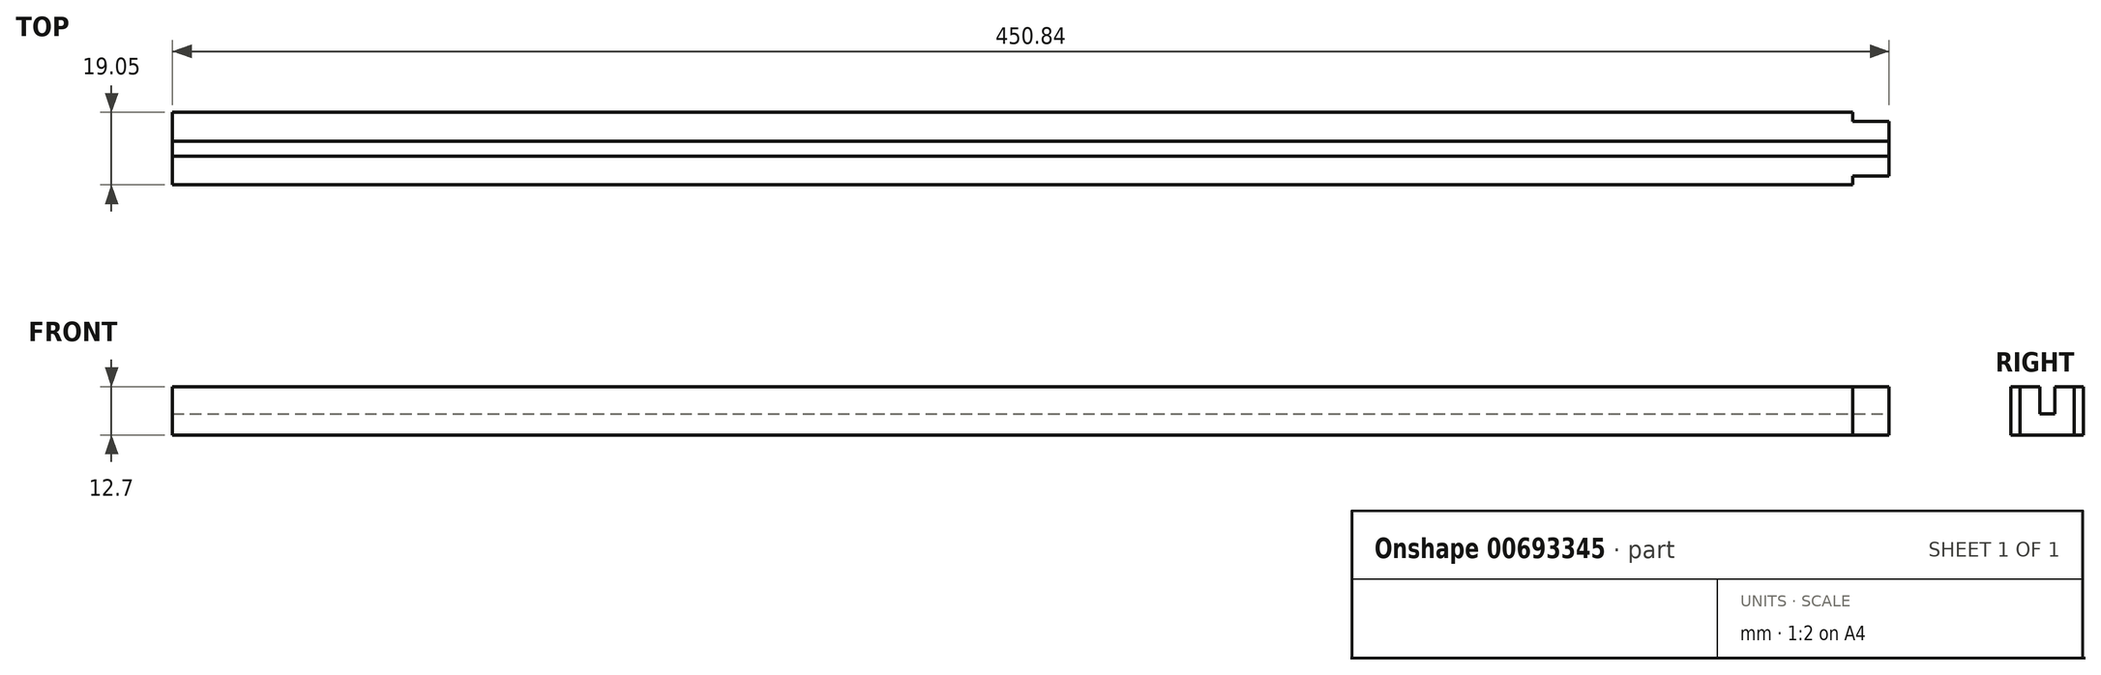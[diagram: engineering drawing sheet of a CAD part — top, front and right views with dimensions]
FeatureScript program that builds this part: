
annotation { "Feature Type Name" : "Feature", "Feature Type Description" : "" }
export const myFeature = defineFeature(function(context is Context, id is Id, definition is map)
    precondition{}
    {
        {
            var Q0;
            Q0=qCreatedBy(makeId("Right.planeOp"),FACE);
            var sketch = newSketch(context, id + "F0", { "sketchPlane" : qUnion([Q0])});
            skLineSegment(sketch, "E0.bottom", {"start": v(0, 0) * mm, "end": v(19.05, 0) * mm});
            skLineSegment(sketch, "E0.top", {"start": v(0, 12.7) * mm, "end": v(19.05, 12.7) * mm});
            skLineSegment(sketch, "E0.left", {"start": v(0, 0) * mm, "end": v(0, 12.7) * mm});
            skLineSegment(sketch, "E0.right", {"start": v(19.05, 0) * mm, "end": v(19.05, 12.7) * mm});
            skSolve(sketch);
        }
        {
            var Q0;
            Q0=qSketchRegion(id+"F0",true);
            extrude(context, id + "F1", {"entities" : qUnion([Q0]), "endBound" : BoundingType.SYMMETRIC, "depth" : 450.85 * mm, "offsetDistance" : 25.4 * mm});
        }
        {
            var Q0;
            Q0=makeQuery(id+"F1.opExtrude","CAP_FACE",FACE,{"disambiguationData":[OSD([sQuery(id+"F0.wireOp",EDGE,"E0.bottom"),sQuery(id+"F0.wireOp",EDGE,"E0.top"),sQuery(id+"F0.wireOp",EDGE,"E0.left"),sQuery(id+"F0.wireOp",EDGE,"E0.right")])],"isStart":false});
            var sketch = newSketch(context, id + "F2", { "sketchPlane" : qUnion([Q0])});
            skLineSegment(sketch, "E1", {"start": v(9.52, 12.7) * mm, "end": v(9.52, 0) * mm, "construction": true});
            skLineSegment(sketch, "E2.bottom", {"start": v(7.54, 12.7) * mm, "end": v(11.5, 12.7) * mm});
            skLineSegment(sketch, "E2.top", {"start": v(7.54, 5.56) * mm, "end": v(11.5, 5.56) * mm});
            skLineSegment(sketch, "E2.left", {"start": v(7.54, 12.7) * mm, "end": v(7.54, 5.56) * mm});
            skLineSegment(sketch, "E2.right", {"start": v(11.5, 12.7) * mm, "end": v(11.5, 5.56) * mm});
            skSolve(sketch);
        }
        {
            var Q0;
            Q0=qSketchRegion(id+"F2",true);
            extrude(context, id + "F3", {"entities" : qUnion([Q0]), "operationType" : NewBodyOperationType.REMOVE, "endBound" : BoundingType.UP_TO_NEXT, "oppositeDirection" : true, "depth" : 25.4 * mm, "offsetDistance" : 25.4 * mm});
        }
        {
            var Q0;
            {var subQ0=sQuery(id+"F0.wireOp",EDGE,"E0.right");var subQ2=sQuery(id+"F0.wireOp",EDGE,"E0.top");Q0=makeQuery(id+"F3.boolean.opBoolean","SPLIT",FACE,{"disambiguationData":[TD([makeQuery(id+"F1.opExtrude","SWEPT_FACE",FACE,{"disambiguationData":[OSD([subQ0])]})])],"derivedFrom":makeQuery(id+"F1.opExtrude","SWEPT_FACE",FACE,{"disambiguationData":[OSD([subQ2])]})});}
            var sketch = newSketch(context, id + "F4", { "sketchPlane" : qUnion([Q0])});
            skLineSegment(sketch, "E3.bottom", {"start": v(215.9, 16.67) * mm, "end": v(225.43, 16.67) * mm});
            skLineSegment(sketch, "E3.top", {"start": v(215.9, 19.05) * mm, "end": v(225.43, 19.05) * mm});
            skLineSegment(sketch, "E3.left", {"start": v(215.9, 16.67) * mm, "end": v(215.9, 19.05) * mm});
            skLineSegment(sketch, "E3.right", {"start": v(225.43, 16.67) * mm, "end": v(225.43, 19.05) * mm});
            skLineSegment(sketch, "E4", {"start": v(225.43, 9.52) * mm, "end": v(222.57, 9.52) * mm, "construction": true});
            skLineSegment(sketch, "E5.MirrorCS", {"start": v(225.43, 2.38) * mm, "end": v(225.43, 0) * mm});
            skLineSegment(sketch, "E6.MirrorCS", {"start": v(215.9, 2.38) * mm, "end": v(215.9, 0) * mm});
            skLineSegment(sketch, "E7.MirrorCS", {"start": v(215.9, 2.38) * mm, "end": v(225.43, 2.38) * mm});
            skLineSegment(sketch, "E8.MirrorCS", {"start": v(215.9, 0) * mm, "end": v(225.43, 0) * mm});
            skSolve(sketch);
        }
        {
            var Q0;
            Q0=qSketchRegion(id+"F4",true);
            extrude(context, id + "F5", {"entities" : qUnion([Q0]), "operationType" : NewBodyOperationType.REMOVE, "endBound" : BoundingType.UP_TO_NEXT, "oppositeDirection" : true, "depth" : 25.4 * mm, "offsetDistance" : 25.4 * mm});
        }
    });
